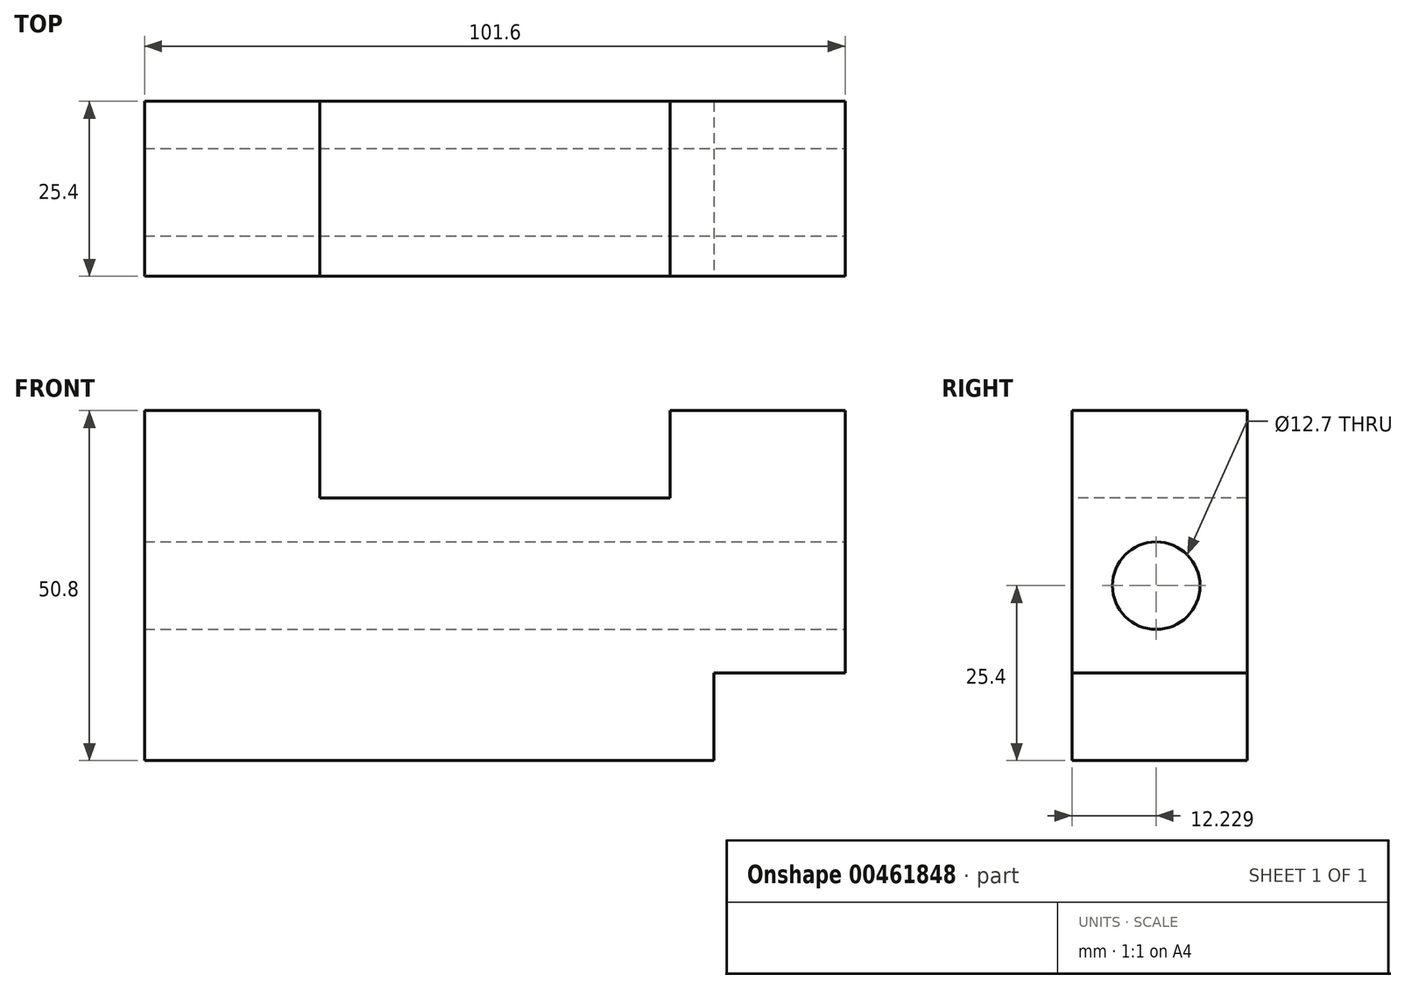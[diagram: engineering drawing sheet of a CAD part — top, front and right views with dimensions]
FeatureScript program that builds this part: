
annotation { "Feature Type Name" : "Feature", "Feature Type Description" : "" }
export const myFeature = defineFeature(function(context is Context, id is Id, definition is map)
    precondition{}
    {
        {
            var Q0;
            Q0=qCreatedBy(makeId("Front.planeOp"),FACE);
            var sketch = newSketch(context, id + "F0", { "sketchPlane" : qUnion([Q0])});
            skLineSegment(sketch, "E0.bottom", {"start": v(-50.8, 25.4) * mm, "end": v(50.8, 25.4) * mm});
            skLineSegment(sketch, "E0.top", {"start": v(-50.8, -25.4) * mm, "end": v(50.8, -25.4) * mm});
            skLineSegment(sketch, "E0.left", {"start": v(-50.8, 25.4) * mm, "end": v(-50.8, -25.4) * mm});
            skLineSegment(sketch, "E0.right", {"start": v(50.8, 25.4) * mm, "end": v(50.8, -25.4) * mm});
            skPoint(sketch, "E0.middle", {"position": v(0, 0) * mm});
            skSolve(sketch);
        }
        {
            var Q0;
            Q0 = qSketchRegion(id + "F0", true);
            extrude(context, id + "F1", {"entities" : qUnion([Q0]), "depth" : 25.4 * mm});
        }
        {
            var Q0;
            Q0=makeQuery(id+"F1.opExtrude","CAP_FACE",FACE,{"disambiguationData":[OSD([sQuery(id+"F0.wireOp",EDGE,"E0.bottom"),sQuery(id+"F0.wireOp",EDGE,"E0.top"),sQuery(id+"F0.wireOp",EDGE,"E0.left"),sQuery(id+"F0.wireOp",EDGE,"E0.right")])],"isStart":false});
            var sketch = newSketch(context, id + "F2", { "sketchPlane" : qUnion([Q0])});
            skLineSegment(sketch, "E1.bottom", {"start": v(-25.4, 25.4) * mm, "end": v(25.4, 25.4) * mm});
            skLineSegment(sketch, "E1.top", {"start": v(-25.4, 12.7) * mm, "end": v(25.4, 12.7) * mm});
            skLineSegment(sketch, "E1.left", {"start": v(-25.4, 25.4) * mm, "end": v(-25.4, 12.7) * mm});
            skLineSegment(sketch, "E1.right", {"start": v(25.4, 25.4) * mm, "end": v(25.4, 12.7) * mm});
            skSolve(sketch);
        }
        {
            var Q0;
            Q0 = qSketchRegion(id + "F2", true);
            extrude(context, id + "F3", {"entities" : qUnion([Q0]), "operationType" : NewBodyOperationType.REMOVE, "endBound" : BoundingType.THROUGH_ALL, "oppositeDirection" : true, "depth" : 25.4 * mm});
        }
        {
            var Q0;
            Q0=makeQuery(id+"F1.opExtrude","CAP_FACE",FACE,{"disambiguationData":[OSD([sQuery(id+"F0.wireOp",EDGE,"E0.bottom"),sQuery(id+"F0.wireOp",EDGE,"E0.top"),sQuery(id+"F0.wireOp",EDGE,"E0.left"),sQuery(id+"F0.wireOp",EDGE,"E0.right")])],"isStart":false});
            var sketch = newSketch(context, id + "F4", { "sketchPlane" : qUnion([Q0])});
            skLineSegment(sketch, "E2.bottom", {"start": v(50.8, -25.4) * mm, "end": v(31.75, -25.4) * mm});
            skLineSegment(sketch, "E2.top", {"start": v(50.8, -12.7) * mm, "end": v(31.75, -12.7) * mm});
            skLineSegment(sketch, "E2.left", {"start": v(50.8, -25.4) * mm, "end": v(50.8, -12.7) * mm});
            skLineSegment(sketch, "E2.right", {"start": v(31.75, -25.4) * mm, "end": v(31.75, -12.7) * mm});
            skSolve(sketch);
        }
        {
            var Q0;
            Q0 = qSketchRegion(id + "F4", true);
            extrude(context, id + "F5", {"entities" : qUnion([Q0]), "operationType" : NewBodyOperationType.REMOVE, "endBound" : BoundingType.THROUGH_ALL, "oppositeDirection" : true, "depth" : 25.4 * mm});
        }
        {
            var Q0;
            Q0=makeQuery(id+"F1.opExtrude","SWEPT_FACE",FACE,{"disambiguationData":[OSD([sQuery(id+"F0.wireOp",EDGE,"E0.right")])]});
            var sketch = newSketch(context, id + "F6", { "sketchPlane" : qUnion([Q0])});
            skCircle(sketch, "E3", {"center": v(-13.17, 0) * mm, "radius": 6.35 * mm});
            skSolve(sketch);
        }
        {
            var Q0;
            Q0 = qSketchRegion(id + "F6", true);
            extrude(context, id + "F7", {"entities" : qUnion([Q0]), "operationType" : NewBodyOperationType.REMOVE, "endBound" : BoundingType.THROUGH_ALL, "oppositeDirection" : true, "depth" : 25.4 * mm});
        }
    });
